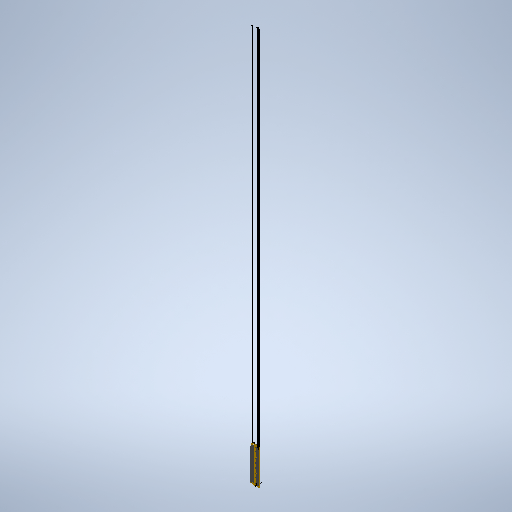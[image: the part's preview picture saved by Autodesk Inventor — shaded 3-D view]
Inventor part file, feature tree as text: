
AUTODESK INVENTOR PART (.ipt)
format: ipt  version: 2025.2 (Build 292293000, 293)  size: 330,752 bytes
history: native  units: mm
features: other x4, extrude x2, sketch x2, pattern_linear x1
ambient origin geometry x8: Origin, YZ Plane, XZ Plane, XY Plane, X Axis, Y Axis, Z Axis, Center Point
bodies: Solid1 (feature_tree)
feature tree (9):
  other  "Annotations"
  extrude  "Extrusion1"  Depth=160.0mm TaperAngle=0.0deg
  extrude  "Extrusion2"  Depth=7.5mm
  pattern_linear  "Rectangular Pattern1"  [2 undecoded]
  sketch  "Sketch_2"  dims[d0=160.0mm d1=0.0mm d2=2.0mm d3=0.0mm]
  sketch  "Sketch_6"  dims[d4=800.0mm d6=22.7mm d7=10.0mm d9=0.0mm d10=2000.0mm d11=7.5mm d12=35.0mm]
  other  "Linear Dimension 1"
  other  "Linear Dimension 2"
  other  "Linear Dimension 3"
note: 2 required parameter values undecoded (feature->parameter linkage not recoverable at this tier; creation-order binding heuristic only, values carry confidence <= 0.55)
